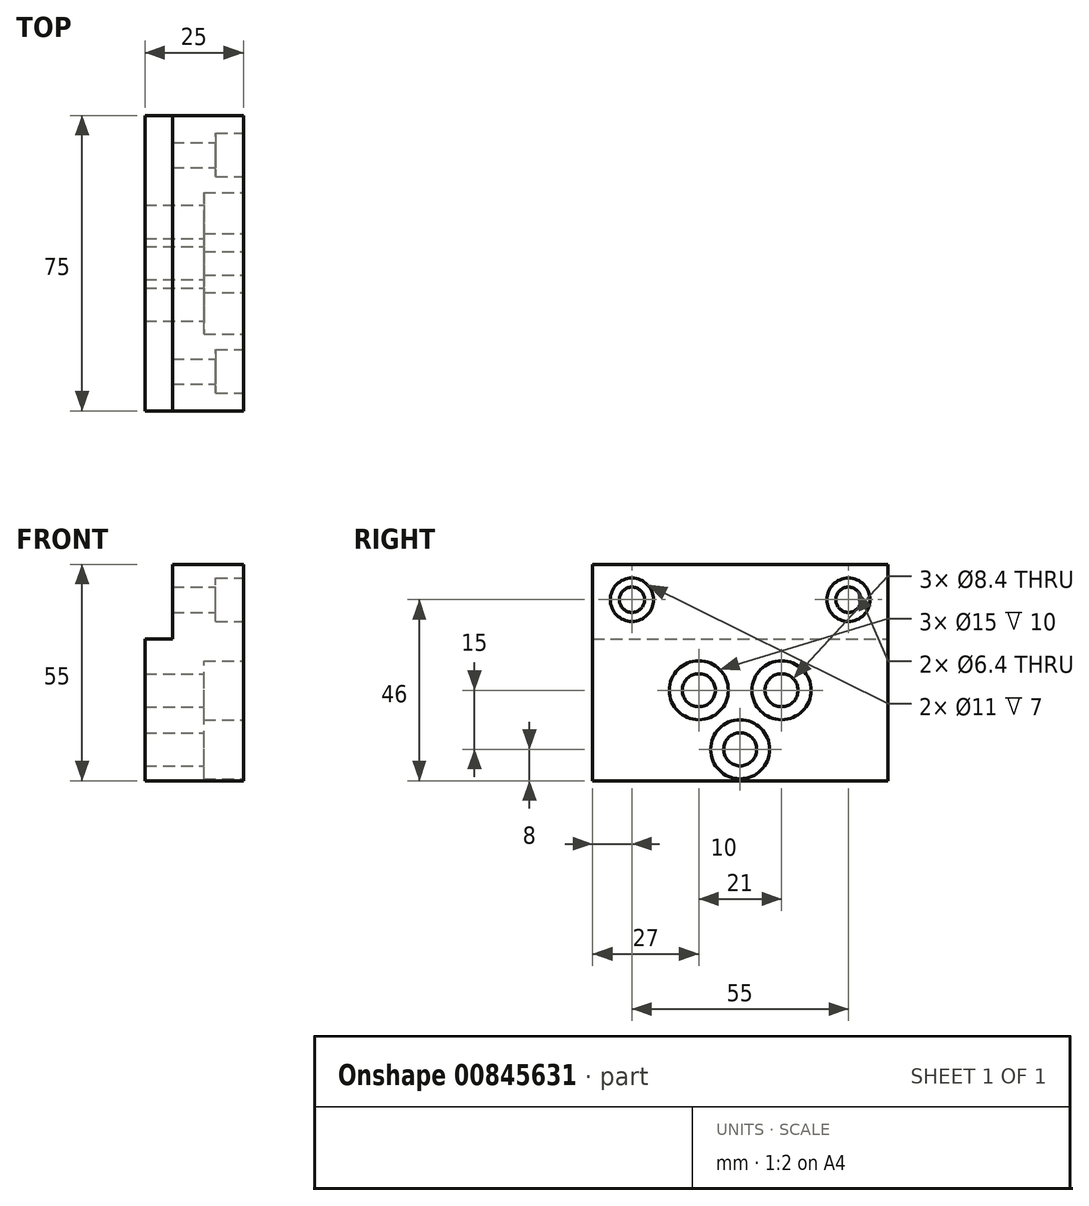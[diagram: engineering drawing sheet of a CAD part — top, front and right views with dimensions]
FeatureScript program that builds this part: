
annotation { "Feature Type Name" : "Feature", "Feature Type Description" : "" }
export const myFeature = defineFeature(function(context is Context, id is Id, definition is map)
    precondition{}
    {
        {
            var Q0;
            Q0=qCreatedBy(makeId("Front.planeOp"),FACE);
            var sketch = newSketch(context, id + "F0", { "sketchPlane" : qUnion([Q0])});
            skLineSegment(sketch, "E0", {"start": v(0, 0) * mm, "end": v(0, 19) * mm});
            skLineSegment(sketch, "E1", {"start": v(0, 19) * mm, "end": v(18, 19) * mm});
            skLineSegment(sketch, "E2", {"start": v(18, 19) * mm, "end": v(18, -36) * mm});
            skLineSegment(sketch, "E3", {"start": v(18, -36) * mm, "end": v(-7, -36) * mm});
            skLineSegment(sketch, "E4", {"start": v(-7, -36) * mm, "end": v(-7, 0) * mm});
            skLineSegment(sketch, "E5", {"start": v(-7, 0) * mm, "end": v(0, 0) * mm});
            skSolve(sketch);
        }
        {
            var Q0;
            Q0=makeQuery(id+"F0.imprint","IMPRINT",FACE,{"disambiguationData":[TD([[makeQuery(id+"F0.imprint","IMPRINT",EDGE,{"derivedFrom":sQuery(id+"F0.wireOp",EDGE,"E0")}),-1.0]])]});
            extrude(context, id + "F1", {"entities" : qUnion([Q0]), "endBound" : BoundingType.SYMMETRIC, "depth" : 75 * mm, "offsetDistance" : 25 * mm});
        }
        {
            var Q0;
            Q0=makeQuery(id+"F1.opExtrude","SWEPT_FACE",FACE,{"disambiguationData":[OSD([sQuery(id+"F0.wireOp",EDGE,"E2")])]});
            var sketch = newSketch(context, id + "F2", { "sketchPlane" : qUnion([Q0])});
            skLineSegment(sketch, "E6", {"start": v(-27.5, 10) * mm, "end": v(27.5, 10) * mm, "construction": true});
            skLineSegment(sketch, "E7", {"start": v(-10.5, -13) * mm, "end": v(10.5, -13) * mm, "construction": true});
            skLineSegment(sketch, "E8", {"start": v(0, -13) * mm, "end": v(0, -28) * mm, "construction": true});
            skSolve(sketch);
        }
        {
            var Q0;
            Q0=sQuery(id+"F2.wireOp",VERTEX,"E7.start");
            var Q1;
            Q1=sQuery(id+"F2.wireOp",VERTEX,"E7.end");
            var Q2;
            Q2=sQuery(id+"F2.wireOp",VERTEX,"E8.end");
            var Q3;
            Q3=makeQuery(id+"F1.opExtrude","SWEPT_BODY",BODY,{"disambiguationData":[OSD([sQuery(id+"F0.wireOp",EDGE,"E0"),sQuery(id+"F0.wireOp",EDGE,"E1"),sQuery(id+"F0.wireOp",EDGE,"E2"),sQuery(id+"F0.wireOp",EDGE,"E3"),sQuery(id+"F0.wireOp",EDGE,"E4"),sQuery(id+"F0.wireOp",EDGE,"E5")])]});
            hole(context, id + "F3", {"style" : HoleStyle.C_BORE, "endStyle" : HoleEndStyle.THROUGH, "holeDiameter" : 8.4 * mm, "cBoreDiameter" : 15 * mm, "cBoreDepth" : 10 * mm, "majorDiameter" : 8 * mm, "isTappedThrough" : true, "tappedDepth" : 17 * mm, "tapClearance" : 3, "startFromSketch" : true, "locations" : qUnion([Q0, Q1, Q2]), "scope" : qUnion([Q3])});
        }
        {
            var Q0;
            Q0=sQuery(id+"F2.wireOp",VERTEX,"E6.start");
            var Q1;
            Q1=sQuery(id+"F2.wireOp",VERTEX,"E6.end");
            var Q2;
            Q2=makeQuery(id+"F1.opExtrude","SWEPT_BODY",BODY,{"disambiguationData":[OSD([sQuery(id+"F0.wireOp",EDGE,"E0"),sQuery(id+"F0.wireOp",EDGE,"E1"),sQuery(id+"F0.wireOp",EDGE,"E2"),sQuery(id+"F0.wireOp",EDGE,"E3"),sQuery(id+"F0.wireOp",EDGE,"E4"),sQuery(id+"F0.wireOp",EDGE,"E5")])]});
            hole(context, id + "F4", {"style" : HoleStyle.C_BORE, "endStyle" : HoleEndStyle.THROUGH, "holeDiameter" : 6.4 * mm, "cBoreDiameter" : 11 * mm, "cBoreDepth" : 7 * mm, "majorDiameter" : 5 * mm, "isTappedThrough" : true, "tappedDepth" : 17 * mm, "tapClearance" : 3, "startFromSketch" : true, "locations" : qUnion([Q0, Q1]), "scope" : qUnion([Q2])});
        }
    });
